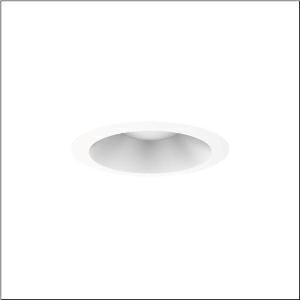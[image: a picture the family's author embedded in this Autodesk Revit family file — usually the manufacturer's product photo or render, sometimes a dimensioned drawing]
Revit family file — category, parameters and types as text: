
# Revit family: lunis_31_midi_51dn16dg32
name_source: partatom
category: Lighting Fixtures
units: mm (PartAtom-declared; Revit-internal decimal feet)

## family parameters
Cut with Voids When Loaded = No
Host = Face
Light Source = No
Part Type = Normal
Room Calculation Point = No
Round Connector Dimension = Use Diameter
Shared = No

## types (1)
- Lunis 31 midi (1 x LED, 2000 lm, 17 W, 3000K)
    Apparent Load = 17 VA
    CIE Flux Codes = 64 93 99 100 100
    Color Rendering = 80
    Color Temperature = 3000K
    Default Elevation = 1800 mm
    Description = Lunis 31,  midi, downlight, light control with reflector, light emission: direct distribution, LED rated luminous flux: 2.000lm, light colour: 830, mains connection: 220..240V, AC, 50/60Hz, housing, white, protection rating (complete): IP20, protection rating (on room side): IP54, insulation class (complete): insulation class II (safety insulation), certification: CE, packaging unit: 1 piece
    Height = 0 mm  [stored 0 ft]
    Lamp = 1 x LED
    Lamp Light Flux = 2000 lm
    Lamp Power = 17 W
    Lamp count = 1
    Length = 259 mm
    Luminous efficacy = 118 lm/W
    Manufacturer = Siteco
    ModVariant = No
    Model = 51DN16DG32
    Mounting Place = Ceiling
    Mounting Type = Recessed
    Number of Poles = 1
    OnlyDefault = Yes
    Power Factor = 1
    Product Name = Lunis 31 midi
    Product group = downlight
    ProductGroupID = 400
    Protection Class = Protection class II
    Protection Degree = IP 20
    RLX_Detail_Level = 1
    RLX_Emergency_Light_Flux = 0 lm
    RLX_Emergency_Type = 0
    RLX_Emergency_Type_DB = No
    RlxData = <blob elided: 23689 chars, md5=a7f367e9>
    Socket = socket
    Standby Power = 0 W
    System Light Flux = 2000 lm
    System Power = 17 W
    Type Comments = Product without accessories
    Type Image = l_1006711.jpg
    URL = http://relux.com
    VarID = ---
    Voltage = 0 V
    Weight = 0.00 kg
    Width = 0 mm  [stored 0 ft]

note: [stored X ft] marks values corroborated as IEEE doubles in the binary element streams (Revit-internal decimal feet)

## geometry (parser evidence)
native form markers: Blend x4, Sweep x12
no freeform markers — native parametric forms only
